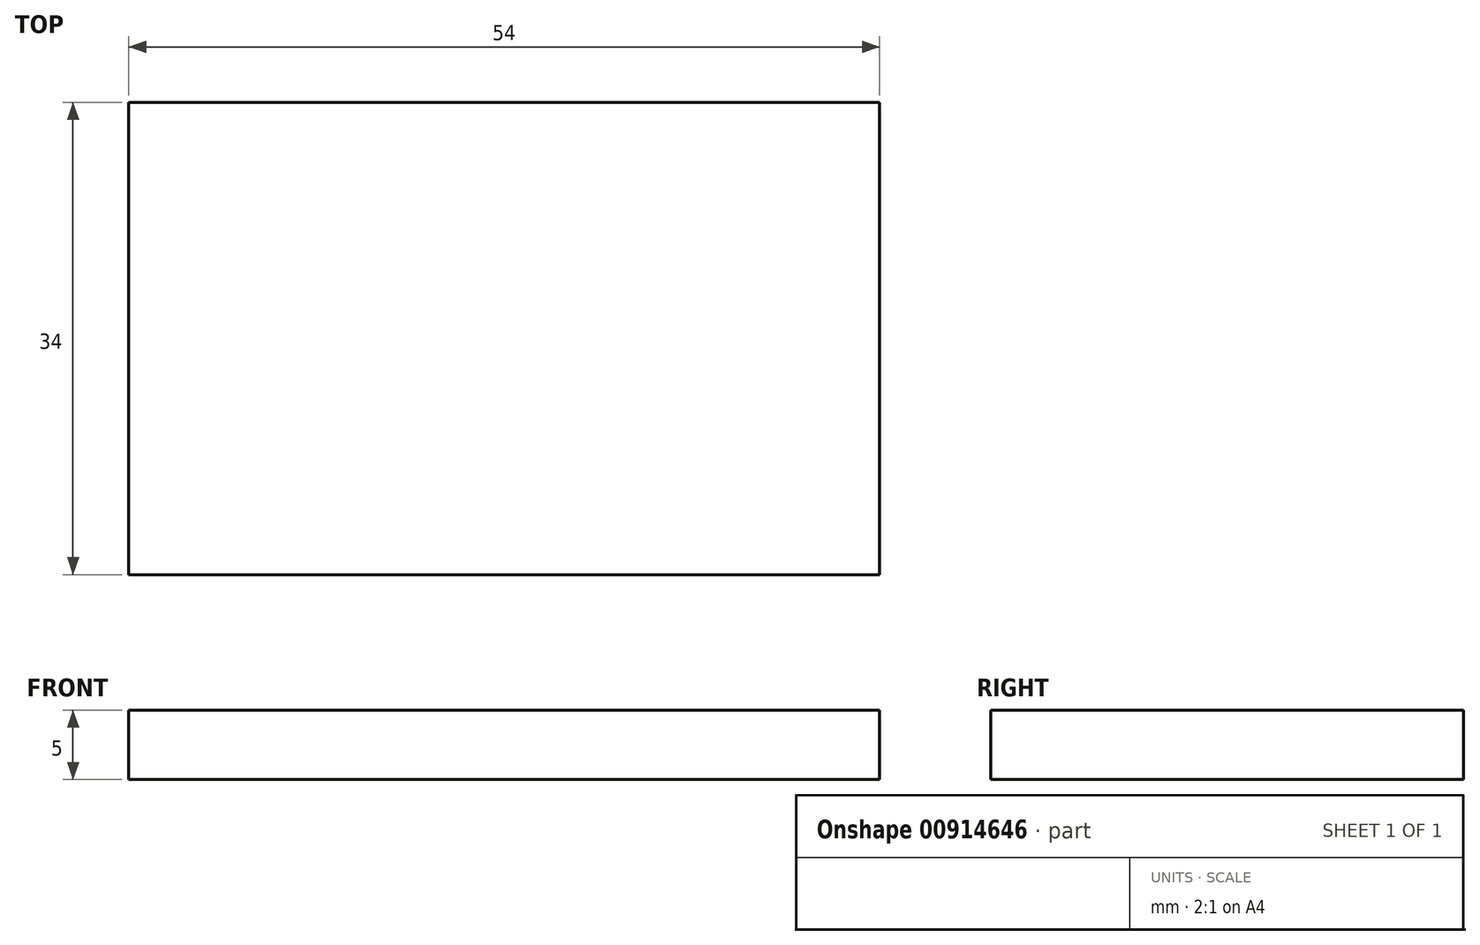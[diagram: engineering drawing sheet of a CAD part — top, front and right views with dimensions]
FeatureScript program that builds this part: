
annotation { "Feature Type Name" : "Feature", "Feature Type Description" : "" }
export const myFeature = defineFeature(function(context is Context, id is Id, definition is map)
    precondition{}
    {
        {
            var Q0;
            Q0=qCreatedBy(makeId("Top.planeOp"),FACE);
            var sketch = newSketch(context, id + "F0", { "sketchPlane" : qUnion([Q0])});
            skLineSegment(sketch, "E0.bottom", {"start": v(-26.33, 12.54) * mm, "end": v(27.67, 12.54) * mm});
            skLineSegment(sketch, "E0.top", {"start": v(-26.33, -21.46) * mm, "end": v(27.67, -21.46) * mm});
            skLineSegment(sketch, "E0.left", {"start": v(-26.33, 12.54) * mm, "end": v(-26.33, -21.46) * mm});
            skLineSegment(sketch, "E0.right", {"start": v(27.67, 12.54) * mm, "end": v(27.67, -21.46) * mm});
            skSolve(sketch);
        }
        {
            var Q0;
            Q0 = qSketchRegion(id + "F0", true);
            extrude(context, id + "F1", {"entities" : qUnion([Q0]), "depth" : 5 * mm, "offsetDistance" : 25 * mm});
        }
    });
